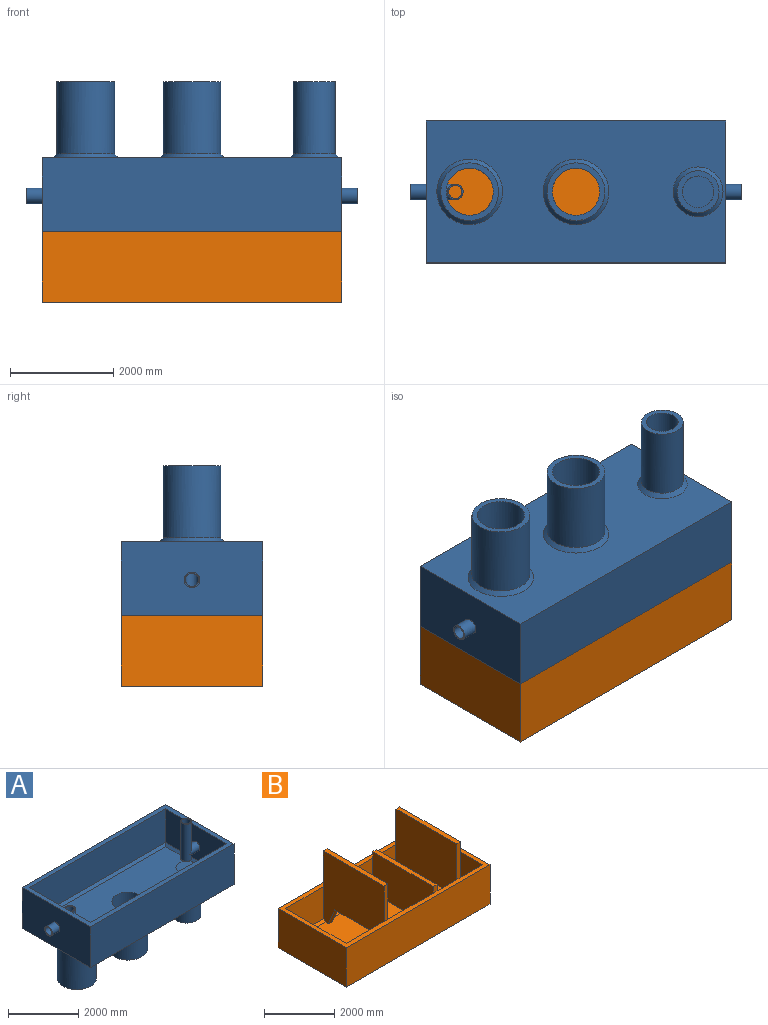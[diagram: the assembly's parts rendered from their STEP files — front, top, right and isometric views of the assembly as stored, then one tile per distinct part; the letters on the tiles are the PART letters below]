
ASSEMBLY  parts=2 mates=1
PART A: 44 faces, bbox 6400.8x2743.2x3276.6 mm
  f0: cylinder r=127mm len=1295.4mm, axis (0,0,-1), area 969167.3mm2, adj f1,f2,f3
  f1: plane 304.8x304.8mm, normal (0,0,1), area 22295.1mm2, adj f0,f4
  f2: cylinder r=127mm len=863.6mm, axis (-1,0,0), area 624606.2mm2, adj f0,f5
  f3: plane 304.8x304.8mm, normal (0,0,-1), area 22295.1mm2, adj f0,f4
  f4: cylinder r=152.4mm len=1295.4mm, axis (0,0,-1), area 1147516.9mm2, adj f1,f3,f6
  f5: plane 304.8x304.8mm, normal (1,0,0), area 22295.1mm2, adj f2,f7
  f6: cylinder r=152.4mm len=406.4mm, axis (1,0,0), area 296248.3mm2, adj f4,f8
  f7: cylinder r=152.4mm len=304.8mm, axis (-1,0,0), area 291863.5mm2, adj f5,f9
  f8: plane 2438.4x1168.4mm, normal (-1,0,0), area 2776060.7mm2, adj f6,f10,f11,f12,f13
  f9: plane 2743.2x1422.4mm, normal (1,0,0), area 3828961.8mm2, adj f7,f13,f14,f15,f16
  f10: plane 5486.4x1168.4mm, normal (0,-1,0), area 6410309.8mm2, adj f8,f13,f17,f18
  f11: plane 2438.4x76.2mm, normal (-0.71,0,0.71), area 254557.9mm2, adj f8,f18,f19,f20
  f12: plane 5486.4x1168.4mm, normal (0,1,0), area 6410309.8mm2, adj f8,f13,f17,f19
  f13: plane 5791.2x2743.2mm, normal (0,0,1), area 2508382.1mm2, adj f8,f9,f10,f12,f15,f16,f17,f21
  f14: plane 5791.2x2743.2mm, normal (0,0,-1), area 12621196.8mm2, adj f9,f15,f16,f21,f22,f23,f24
  f15: plane 5791.2x1422.4mm, normal (0,1,0), area 8237402.9mm2, adj f9,f13,f14,f21
  f16: plane 5791.2x1422.4mm, normal (0,-1,0), area 8237402.9mm2, adj f9,f13,f14,f21
  f17: plane 2438.4x1168.4mm, normal (1,0,0), area 2776060.7mm2, adj f10,f12,f13,f25,f26
  f18: plane 5486.4x76.2mm, normal (0,-0.71,0.71), area 583019.8mm2, adj f10,f11,f20,f26
  f19: plane 5486.4x76.2mm, normal (0,0.71,0.71), area 583019.8mm2, adj f11,f12,f20,f26
  f20: plane 5334x2286mm, normal (0,0,1), area 10880138.2mm2, adj f11,f18,f19,f26,f27,f28
  f21: plane 2743.2x1422.4mm, normal (-1,0,0), area 3828961.8mm2, adj f13,f14,f15,f16,f29
  f22: cone r=406.4mm half-angle=45deg, axis (0,0,1), area 300968.9mm2, adj f14,f30
  f23: cone r=558.8mm half-angle=45deg, axis (0,0,1), area 404158.2mm2, adj f14,f31
  f24: cone r=558.8mm half-angle=45deg, axis (0,0,1), area 404158.2mm2, adj f14,f32
  f25: cylinder r=152.4mm len=406.4mm, axis (-1,0,0), area 296248.3mm2, adj f17,f33
  f26: plane 2438.4x76.2mm, normal (0.71,0,0.71), area 254557.9mm2, adj f17,f18,f19,f20
  f27: cylinder r=457.2mm len=1651mm, axis (0,0,1), area 4742782mm2, adj f20,f34
  f28: cylinder r=457.2mm len=1651mm, axis (0,0,1), area 4742782mm2, adj f20,f35
  f29: cylinder r=152.4mm len=304.8mm, axis (1,0,0), area 291863.5mm2, adj f21,f36
  f30: cylinder r=406.4mm len=1397mm, axis (0,0,1), area 3567220.7mm2, adj f22,f37
  f31: cylinder r=558.8mm len=1397mm, axis (0,0,1), area 4904928.4mm2, adj f23,f35
  f32: cylinder r=558.8mm len=1397mm, axis (0,0,1), area 4904928.4mm2, adj f24,f34
  f33: cylinder r=152.4mm len=584.2mm, axis (0,0,-1), area 466502.1mm2, adj f25,f38,f39
  f34: plane 1117.6x1117.6mm, normal (0,0,-1), area 324292.8mm2, adj f27,f32
  f35: plane 1117.6x1117.6mm, normal (0,0,-1), area 324292.8mm2, adj f28,f31
  f36: plane 304.8x304.8mm, normal (-1,0,0), area 22295.1mm2, adj f29,f40
  f37: plane 812.8x812.8mm, normal (0,0,-1), area 227005mm2, adj f30,f41
  f38: plane 304.8x304.8mm, normal (0,0,1), area 22295.1mm2, adj f33,f42
  f39: plane 304.8x304.8mm, normal (0,0,-1), area 22295.1mm2, adj f33,f42
  f40: cylinder r=127mm len=863.6mm, axis (-1,0,0), area 624606.2mm2, adj f36,f42
  f41: cylinder r=304.8mm len=1651mm, axis (0,0,1), area 3161854.7mm2, adj f37,f43
  f42: cylinder r=127mm len=584.2mm, axis (0,0,-1), area 401654.9mm2, adj f38,f39,f40
  f43: plane 609.6x609.6mm, normal (0,0,-1), area 291863.5mm2, adj f41
PART B: 49 faces, bbox 5791.2x2743.2x2616.2 mm
  f0: plane 1828.8x1117.6mm, normal (0,-1,0), area 2043866.9mm2, adj f17,f24,f38,f48
  f1: plane 1828.8x1117.6mm, normal (0,1,0), area 2043866.9mm2, adj f17,f24,f38,f44
  f2: plane 3429x2286mm, normal (0,0,1), area 7799984.4mm2, adj f20,f22,f24,f25,f38,f44,f45,f46
  f3: plane 1117.6x787.4mm, normal (0,-1,0), area 879998.2mm2, adj f17,f32,f37,f42
  f4: plane 1117.6x787.4mm, normal (0,1,0), area 879998.2mm2, adj f17,f32,f37,f43
  f5: plane 1524x1117.6mm, normal (0,-1,0), area 1703222.4mm2, adj f13,f17,f25,f45
  f6: plane 1524x1117.6mm, normal (0,1,0), area 1703222.4mm2, adj f13,f17,f25,f47
  f7: plane 2286x1752.6mm, normal (0,0,1), area 3967734mm2, adj f28,f30,f32,f33,f37,f39,f40,f41
  f8: plane 2743.2x1371.6mm, normal (-1,0,0), area 3762573.1mm2, adj f9,f11,f12,f17
  f9: plane 5791.2x1371.6mm, normal (0,-1,0), area 7943209.9mm2, adj f8,f10,f12,f17
  f10: plane 2743.2x1371.6mm, normal (1,0,0), area 3762573.1mm2, adj f9,f11,f12,f17
  f11: plane 5791.2x1371.6mm, normal (0,1,0), area 7943209.9mm2, adj f8,f10,f12,f17
  f12: plane 5791.2x2743.2mm, normal (0,0,-1), area 15886419.8mm2, adj f8,f9,f10,f11
  f13: plane 2438.4x1117.6mm, normal (1,0,0), area 2725155.8mm2, adj f5,f6,f17,f46
  f14: plane 1117.6x889mm, normal (0,-1,0), area 993546.4mm2, adj f15,f17,f33,f41
  f15: plane 2438.4x1117.6mm, normal (-1,0,0), area 2725155.8mm2, adj f14,f16,f17,f40
  f16: plane 1117.6x889mm, normal (0,1,0), area 993546.4mm2, adj f15,f17,f33,f39
  f17: plane 5791.2x2743.2mm, normal (0,0,1), area 2508382.1mm2, adj f0,f1,f3,f4,f5,f6,f8,f9
  f18: plane 1244.6x152.4mm, normal (0,1,0), area 189677mm2, adj f17,f21,f24,f25
  f19: plane 1244.6x152.4mm, normal (0,-1,0), area 189677mm2, adj f17,f21,f24,f25
  f20: plane 609.6x254mm, normal (0,-0.92,-0.38), area 100645mm2, adj f2,f23,f24,f25
  f21: plane 2438.4x152.4mm, normal (0,0,1), area 371612.2mm2, adj f18,f19,f24,f25
  f22: plane 609.6x254mm, normal (0,0.92,-0.38), area 100645mm2, adj f2,f23,f24,f25
  f23: plane 1524x152.4mm, normal (0,0,-1), area 232257.6mm2, adj f20,f22,f24,f25
  f24: plane 2438.4x2438.4mm, normal (1,0,0), area 4856119.3mm2, adj f0,f1,f2,f18,f19,f20,f21,f22
  f25: plane 2438.4x2438.4mm, normal (-1,0,0), area 4856119.3mm2, adj f2,f5,f6,f18,f19,f20,f21,f22
  f26: plane 2438.4x152.4mm, normal (0,0,1), area 371612.2mm2, adj f27,f31,f32,f33
  f27: plane 1244.6x152.4mm, normal (0,1,0), area 189677mm2, adj f17,f26,f32,f33
  f28: plane 609.6x254mm, normal (0,-0.92,-0.38), area 100645mm2, adj f7,f29,f32,f33
  f29: plane 1524x152.4mm, normal (0,0,-1), area 232257.6mm2, adj f28,f30,f32,f33
  f30: plane 609.6x254mm, normal (0,0.92,-0.38), area 100645mm2, adj f7,f29,f32,f33
  f31: plane 1244.6x152.4mm, normal (0,-1,0), area 189677mm2, adj f17,f26,f32,f33
  f32: plane 2438.4x2438.4mm, normal (-1,0,0), area 4856119.3mm2, adj f3,f4,f7,f26,f27,f28,f29,f30
  f33: plane 2438.4x2438.4mm, normal (1,0,0), area 4856119.3mm2, adj f7,f14,f16,f26,f27,f28,f29,f30
  f34: plane 228.6x152.4mm, normal (0,1,0), area 34838.6mm2, adj f17,f36,f37,f38
  f35: plane 228.6x152.4mm, normal (0,-1,0), area 34838.6mm2, adj f17,f36,f37,f38
  f36: plane 2438.4x152.4mm, normal (0,0,1), area 371612.2mm2, adj f34,f35,f37,f38
  f37: plane 2438.4x1422.4mm, normal (1,0,0), area 3462573.7mm2, adj f3,f4,f7,f34,f35,f36,f42,f43
  f38: plane 2438.4x1422.4mm, normal (-1,0,0), area 3462573.7mm2, adj f0,f1,f2,f34,f35,f36,f44,f48
  f39: plane 889x76.2mm, normal (0,0.71,0.71), area 91695.6mm2, adj f7,f16,f33,f40
  f40: plane 2438.4x76.2mm, normal (-0.71,0,0.71), area 254557.9mm2, adj f7,f15,f39,f41
  f41: plane 889x76.2mm, normal (0,-0.71,0.71), area 91695.6mm2, adj f7,f14,f33,f40
  f42: plane 787.4x76.2mm, normal (0,-0.71,0.71), area 84852.6mm2, adj f3,f7,f32,f37
  f43: plane 787.4x76.2mm, normal (0,0.71,0.71), area 84852.6mm2, adj f4,f7,f32,f37
  f44: plane 1828.8x76.2mm, normal (0,0.71,0.71), area 197077.1mm2, adj f1,f2,f24,f38
  f45: plane 1524x76.2mm, normal (0,-0.71,0.71), area 160125.2mm2, adj f2,f5,f25,f46
  f46: plane 2438.4x76.2mm, normal (0.71,0,0.71), area 254557.9mm2, adj f2,f13,f45,f47
  f47: plane 1524x76.2mm, normal (0,0.71,0.71), area 160125.2mm2, adj f2,f6,f25,f46
  f48: plane 1828.8x76.2mm, normal (0,-0.71,0.71), area 197077.1mm2, adj f0,f2,f24,f38
PLACE A rot(axis=(1,0,0),180deg) t=(539.34,5425.31,4591.73)mm
PLACE B t=(539.34,2682.11,1797.73)mm fixed
MATE fastened A.f13 <-> B.f17  axis (0,0,-1) through (6330.54,5425.31,3169.33)mm
